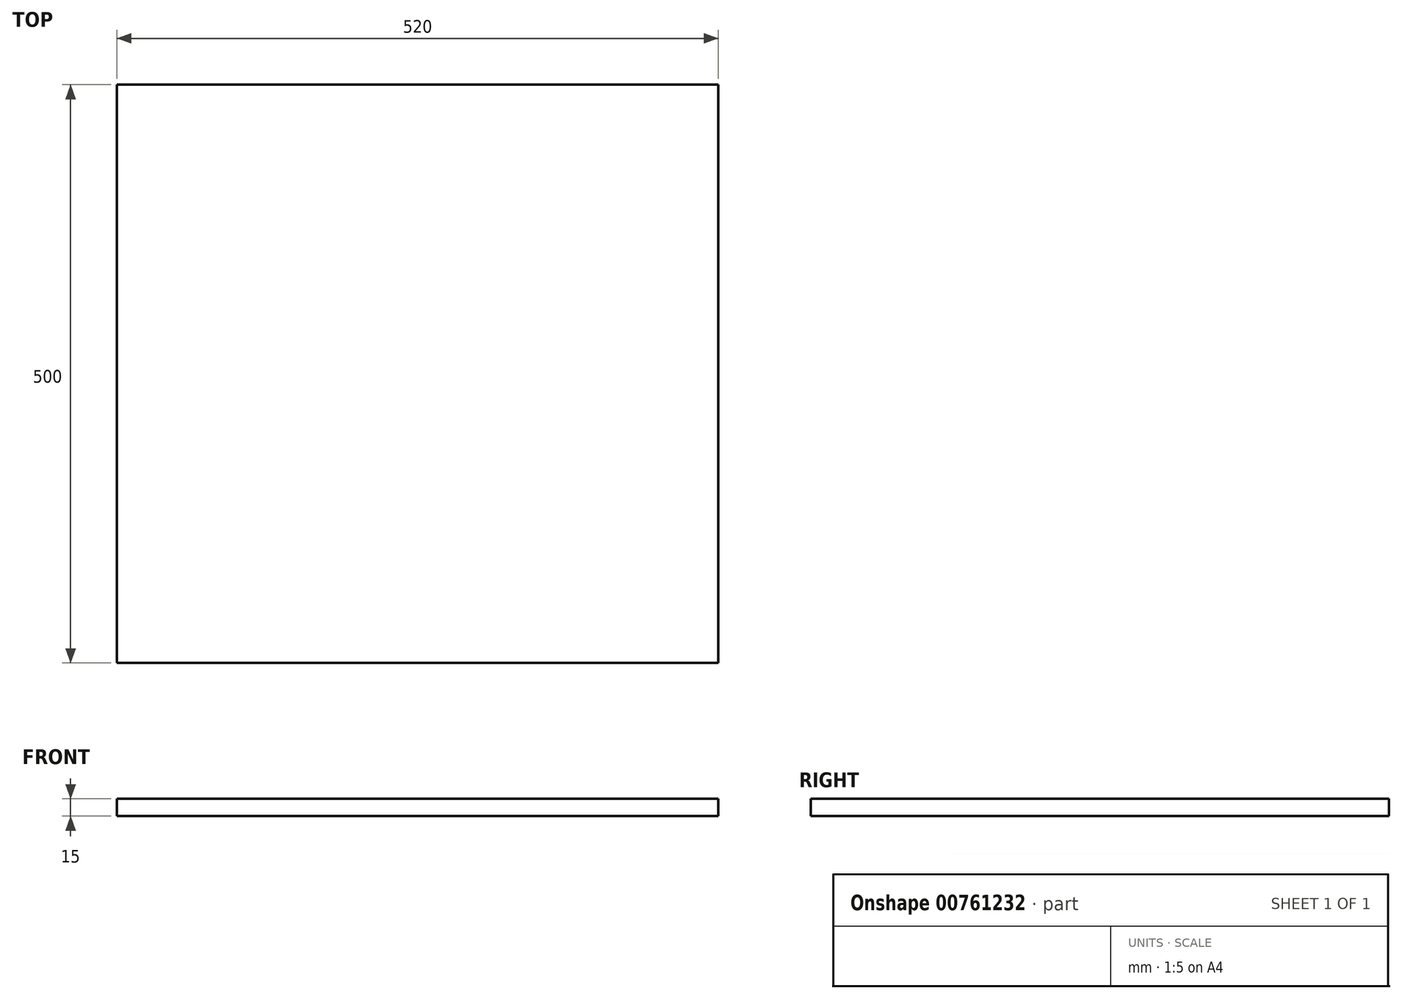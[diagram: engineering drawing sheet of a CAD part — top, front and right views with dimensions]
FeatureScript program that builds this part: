
annotation { "Feature Type Name" : "Feature", "Feature Type Description" : "" }
export const myFeature = defineFeature(function(context is Context, id is Id, definition is map)
    precondition{}
    {
        {
            var Q0;
            Q0=qCreatedBy(makeId("Front.planeOp"),FACE);
            var sketch = newSketch(context, id + "F0", { "sketchPlane" : qUnion([Q0])});
            skLineSegment(sketch, "E0.bottom", {"start": v(260, 7.5) * mm, "end": v(-260, 7.5) * mm});
            skLineSegment(sketch, "E0.top", {"start": v(260, -7.5) * mm, "end": v(-260, -7.5) * mm});
            skLineSegment(sketch, "E0.left", {"start": v(260, 7.5) * mm, "end": v(260, -7.5) * mm});
            skLineSegment(sketch, "E0.right", {"start": v(-260, 7.5) * mm, "end": v(-260, -7.5) * mm});
            skPoint(sketch, "E0.middle", {"position": v(0, 0) * mm});
            skSolve(sketch);
        }
        {
            var Q0;
            Q0=makeQuery(id+"F0.imprint","IMPRINT",FACE,{"disambiguationData":[TD([[makeQuery(id+"F0.imprint","IMPRINT",EDGE,{"derivedFrom":sQuery(id+"F0.wireOp",EDGE,"E0.bottom")}),1.0]])]});
            extrude(context, id + "F1", {"entities" : qUnion([Q0]), "endBound" : BoundingType.SYMMETRIC, "depth" : 500 * mm, "offsetDistance" : 25 * mm});
        }
    });
